annotation { "Feature Type Name" : "Feature", "Feature Type Description" : "" }
export const myFeature = defineFeature(function(context is Context, id is Id, definition is map)
    precondition{}
    {
        {
            var Q0;
            Q0=qCreatedBy(makeId("Top.planeOp"),FACE);
            var sketch = newSketch(context, id + "F0", { "sketchPlane" : qUnion([Q0])});
            skLineSegment(sketch, "E0.bottom", {"start": v(-16.97, -43.24) * mm, "end": v(16.97, -43.24) * mm});
            skLineSegment(sketch, "E0.top", {"start": v(-16.97, 43.24) * mm, "end": v(-7.19, 43.24) * mm});
            skLineSegment(sketch, "E0.left", {"start": v(-16.97, -43.24) * mm, "end": v(-16.97, 43.24) * mm});
            skLineSegment(sketch, "E0.right", {"start": v(16.97, -43.24) * mm, "end": v(16.97, 43.24) * mm});
            skLineSegment(sketch, "E1.bottom", {"start": v(-7.19, 55.82) * mm, "end": v(7.19, 55.82) * mm});
            skLineSegment(sketch, "E1.left", {"start": v(-7.19, 55.82) * mm, "end": v(-7.19, 43.24) * mm});
            skLineSegment(sketch, "E1.right", {"start": v(7.19, 55.82) * mm, "end": v(7.19, 43.24) * mm});
            skLineSegment(sketch, "E2.trimOffspring", {"start": v(7.19, 43.24) * mm, "end": v(16.97, 43.24) * mm});
            skSolve(sketch);
        }
        {
            var Q0;
            Q0=qCreatedBy(makeId("Top.planeOp"),FACE);
            var sketch = newSketch(context, id + "F1", { "sketchPlane" : qUnion([Q0])});
            skLineSegment(sketch, "E3.bottom", {"start": v(-19.05, -44.97) * mm, "end": v(19.05, -44.97) * mm});
            skLineSegment(sketch, "E3.top", {"start": v(-19.05, 57.54) * mm, "end": v(19.05, 57.54) * mm});
            skLineSegment(sketch, "E3.left", {"start": v(-19.05, -44.97) * mm, "end": v(-19.05, 57.54) * mm});
            skLineSegment(sketch, "E3.right", {"start": v(19.05, -44.97) * mm, "end": v(19.05, 57.54) * mm});
            skSolve(sketch);
        }
        {
            var Q0;
            Q0=qCreatedBy(makeId("Top.planeOp"),FACE);
            var sketch = newSketch(context, id + "F2", { "sketchPlane" : qUnion([Q0])});
            skLineSegment(sketch, "E4", {"start": v(10.92, -0.52) * mm, "end": v(10.92, -18.3) * mm, "construction": true});
            skArc(sketch, "E5", {"start": v(13.46, -0.52) * mm, "mid": v(10.92, 2.02) * mm, "end": v(8.38, -0.52) * mm});
            skArc(sketch, "E6", {"start": v(8.38, -18.3) * mm, "mid": v(10.92, -20.84) * mm, "end": v(13.46, -18.3) * mm});
            skLineSegment(sketch, "E7", {"start": v(8.38, -0.52) * mm, "end": v(8.38, -18.3) * mm});
            skLineSegment(sketch, "E8", {"start": v(13.46, -0.52) * mm, "end": v(13.46, -18.3) * mm});
            skSolve(sketch);
        }
        {
            var Q0;
            Q0=qCreatedBy(makeId("Front.planeOp"),FACE);
            var sketch = newSketch(context, id + "F3", { "sketchPlane" : qUnion([Q0])});
            skPoint(sketch, "E9.0", {"position": v(-19.05, 0) * mm});
            skPoint(sketch, "E10.0", {"position": v(19.05, 0) * mm});
            skLineSegment(sketch, "E11", {"start": v(-19.05, 0) * mm, "end": v(19.05, 0) * mm});
            skLineSegment(sketch, "E12", {"start": v(-19.05, 0) * mm, "end": v(-19.05, 27.26) * mm});
            skLineSegment(sketch, "E13", {"start": v(19.05, 0) * mm, "end": v(19.05, 27.26) * mm});
            skArc(sketch, "E14", {"start": v(13.36, 31.23) * mm, "mid": v(0, 33.02) * mm, "end": v(-13.36, 31.23) * mm});
            skPoint(sketch, "E15", {"position": v(0, 33.02) * mm});
            skArc(sketch, "E16", {"start": v(-16.71, 30.32) * mm, "mid": v(-18.4, 29.18) * mm, "end": v(-19.05, 27.26) * mm});
            skArc(sketch, "E17.MirrorCS", {"start": v(16.71, 30.32) * mm, "mid": v(18.4, 29.18) * mm, "end": v(19.05, 27.26) * mm});
            skLineSegment(sketch, "E18", {"start": v(-13.36, 31.23) * mm, "end": v(-16.71, 30.32) * mm});
            skLineSegment(sketch, "E19", {"start": v(13.36, 31.23) * mm, "end": v(16.71, 30.32) * mm});
            skSolve(sketch);
        }
        {
            var Q0;
            Q0=makeQuery(id+"F3.imprint","IMPRINT",FACE,{"disambiguationData":[TD([[makeQuery(id+"F3.imprint","IMPRINT",EDGE,{"derivedFrom":sQuery(id+"F3.wireOp",EDGE,"E11")}),1.0]])]});
            var Q1;
            Q1=sQuery(id+"F1.wireOp",VERTEX,"E3.bottom.start");
            var Q2;
            Q2=sQuery(id+"F1.wireOp",VERTEX,"E3.left.end");
            extrude(context, id + "F4", {"entities" : qUnion([Q0]), "endBound" : BoundingType.UP_TO_VERTEX, "depth" : 25.4 * mm, "endBoundEntityVertex" : qUnion([Q1]), "offsetDistance" : 25.4 * mm, "hasSecondDirection" : true, "secondDirectionBound" : SecondDirectionBoundingType.UP_TO_VERTEX, "secondDirectionOppositeDirection" : true, "secondDirectionDepth" : 25.4 * mm, "secondDirectionBoundEntityVertex" : qUnion([Q2])});
        }
        {
            var Q0;
            Q0=makeQuery(id+"F4.opExtrude","SWEPT_FACE",FACE,{"disambiguationData":[OSD([sQuery(id+"F3.wireOp",EDGE,"E11")])]});
            shell(context, id + "F5", {"entities" : qUnion([Q0]), "thickness" : 2 * mm});
        }
        {
            var Q0;
            Q0=qSketchRegion(id+"F2",true);
            extrude(context, id + "F6", {"entities" : qUnion([Q0]), "operationType" : NewBodyOperationType.REMOVE, "endBound" : BoundingType.THROUGH_ALL, "depth" : 25.4 * mm, "offsetDistance" : 25.4 * mm});
        }
        {
            var Q0;
            Q0=makeQuery(id+"F4.opExtrude","CAP_FACE",FACE,{"disambiguationData":[OSD([sQuery(id+"F3.wireOp",EDGE,"E11"),sQuery(id+"F3.wireOp",EDGE,"E12"),sQuery(id+"F3.wireOp",EDGE,"E13"),sQuery(id+"F3.wireOp",EDGE,"E14"),sQuery(id+"F3.wireOp",EDGE,"E16"),sQuery(id+"F3.wireOp",EDGE,"E17.MirrorCS"),sQuery(id+"F3.wireOp",EDGE,"E18"),sQuery(id+"F3.wireOp",EDGE,"E19")])],"isStart":true});
            var sketch = newSketch(context, id + "F7", { "sketchPlane" : qUnion([Q0])});
            skCircle(sketch, "E20", {"center": v(0, 17.09) * mm, "radius": 11.11 * mm});
            skSolve(sketch);
        }
        {
            var Q0;
            Q0=makeQuery(id+"F7.imprint","IMPRINT",FACE,{"disambiguationData":[TD([[makeQuery(id+"F7.imprint","IMPRINT",EDGE,{"derivedFrom":sQuery(id+"F7.wireOp",EDGE,"E20")}),1.0]])]});
            extrude(context, id + "F8", {"entities" : qUnion([Q0]), "operationType" : NewBodyOperationType.ADD, "depth" : 2 * mm, "offsetDistance" : 25.4 * mm});
        }
        {
            var Q0;
            Q0=makeQuery(id+"F4.opExtrude","SWEPT_FACE",FACE,{"disambiguationData":[OSD([sQuery(id+"F3.wireOp",EDGE,"E12")])]});
            var sketch = newSketch(context, id + "F9", { "sketchPlane" : qUnion([Q0])});
            skText(sketch, "E21", { "text": "Jacob Express", "fontName": "OpenSans-Regular.ttf"});
            const initialGuessF9  = {"E21": [-0.05188, 0.00907, 1, 0, 0.01016]};
            skSetInitialGuess(sketch, initialGuessF9);
            skSolve(sketch);
        }
        {
            var Q0;
            Q0 = qSketchRegion(id + "F9", true);
            extrude(context, id + "F10", {"entities" : qUnion([Q0]), "operationType" : NewBodyOperationType.ADD, "depth" : 1 * mm, "offsetDistance" : 25.4 * mm});
        }
        {
            var Q0;
            Q0=makeQuery(id+"F4.opExtrude","SWEPT_FACE",FACE,{"disambiguationData":[OSD([sQuery(id+"F3.wireOp",EDGE,"E13")])]});
            var sketch = newSketch(context, id + "F11", { "sketchPlane" : qUnion([Q0])});
            skText(sketch, "E22", { "text": "Jacob Express", "fontName": "OpenSans-Regular.ttf"});
            const initialGuessF11  = {"E22": [-0.03912, 0.00898, 1, 0, 0.01016]};
            skSetInitialGuess(sketch, initialGuessF11);
            skSolve(sketch);
        }
        {
            var Q0;
            Q0 = qSketchRegion(id + "F11", true);
            extrude(context, id + "F12", {"entities" : qUnion([Q0]), "operationType" : NewBodyOperationType.ADD, "depth" : 1 * mm, "offsetDistance" : 25.4 * mm});
        }
    });